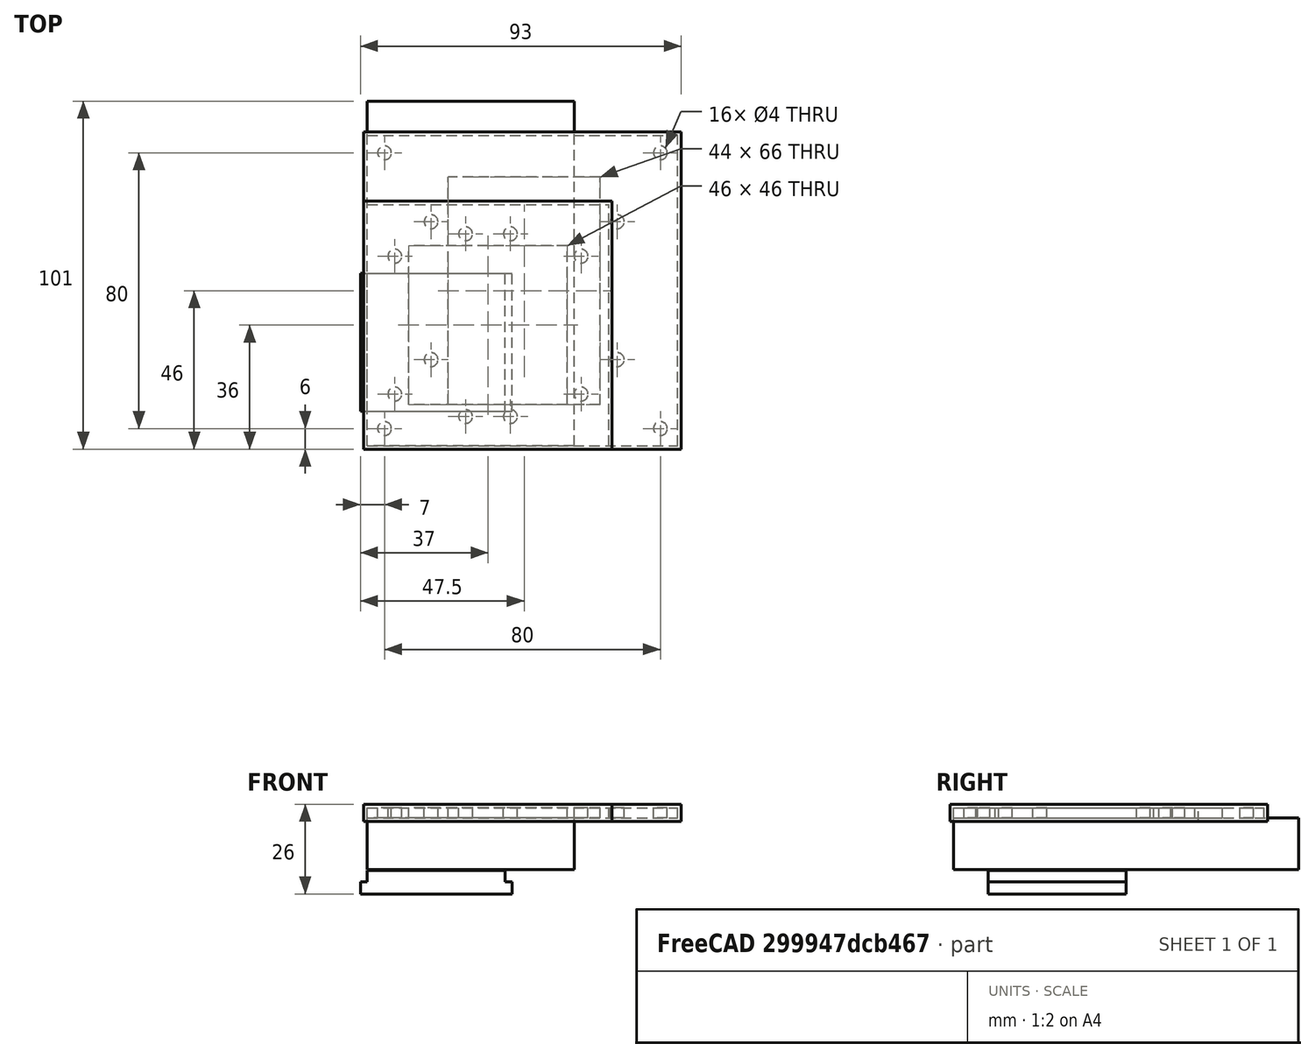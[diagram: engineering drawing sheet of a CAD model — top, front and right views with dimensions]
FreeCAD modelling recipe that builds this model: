
FCSTD DOCUMENT  (FreeCAD 0.18.4R)
Label: box_with_cone
License: All rights reserved
LicenseURL: http://en.wikipedia.org/wiki/All_rights_reserved
objects: Path::FeaturePython×20, Part::FeaturePython×12, Part::Box×8, Part::Cut×6, Part::Cylinder×5, Part::MultiFuse×4, App::Part×4, App::FeaturePython×3, App::DocumentObjectGroup×3, Path::FeatureCompoundPython×3, Part::Cone×2, Part::Feature×2, Part::Fuse×1
note: 47 computed .brp shape members not serialized (recipe doc carries the construction recipe); baked Part::Feature solids carry a one-line shape summary decoded from their .brp

FEATURE [Part::Box] Box  label="Cube"
  AttacherType = Attacher::AttachEngine3D
  Height = 15
  Length = 40
  Placement = pos=(0,0,-15) rot=(0,0,1;0rad)
  Width = 60
FEATURE [Part::Cone] Cone  label="top cone"
  Angle = 360
  AttacherType = Attacher::AttachEngine3D
  Height = 7
  Placement = pos=(0,0,-7) rot=(0,0,1;0rad)
  Radius1 = 2.8
  Radius2 = 3
FEATURE [Part::Cone] Cone001  label="bottom cone"
  Angle = 360
  AttacherType = Attacher::AttachEngine3D
  Height = 12
  Placement = pos=(0,0,-19) rot=(0,0,1;3.14159rad)
  Radius1 = 1.2
  Radius2 = 2.8
  Support = -> [Cone]
FEATURE [Part::Cylinder] Cylinder001
  Angle = 360
  AttacherType = Attacher::AttachEngine3D
  Height = 30
  Placement = pos=(0,0,-20) rot=(0,0,1;0rad)
  Radius = 1.65
FEATURE [Part::FeaturePython] Array002  # Draft array (typed FeaturePython)
  Angle = 360
  ArrayType = 0
  Axis = (0,0,1)
  Base = -> Cylinder001
  Center = (0,0,0)
  Fuse = false
  IntervalAxis = (0,0,0)
  IntervalX = (13,0,0)
  IntervalY = (0,53,0)
  IntervalZ = (0,0,1)
  NumberPolar = 1
  NumberX = 2
  NumberY = 2
  NumberZ = 1
  Placement = pos=(13.5,3.5,0) rot=(0,0,1;0rad)
FEATURE [Part::Fuse] Fusion
  Base = -> Cone001
  Placement = pos=(0,0,5) rot=(0,0,1;0rad)
  Tool = -> Cone
FEATURE [Part::FeaturePython] Array  label="cone array"  # Draft array (typed FeaturePython)
  Angle = 360
  ArrayType = 0
  Axis = (0,0,1)
  Base = -> Fusion
  Center = (0,0,0)
  Fuse = false
  IntervalAxis = (0,0,0)
  IntervalX = (13,0,0)
  IntervalY = (0,13,0)
  IntervalZ = (0,0,1)
  NumberPolar = 1
  NumberX = 3
  NumberY = 4
  NumberZ = 1
  Placement = pos=(7,10,0) rot=(0,0,1;0rad)
FEATURE [Part::Cut] Cut  label="cut cones"
  Base = -> Box
  Tool = -> Array
FEATURE [Part::Box] Box001  label="aluminium solid"
  AttacherType = Attacher::AttachEngine3D
  Height = 15
  Length = 100
  Placement = pos=(0,0,-15) rot=(0,0,1;0rad)
  Width = 60
FEATURE [App::FeaturePython] SetupSheet  # Path/CAM operation (typed FeaturePython)
  ClearanceHeightExpression = OpStockZMax+SetupSheet.ClearanceHeightOffset
  ClearanceHeightOffset = 5
  FinalDepthExpression = OpFinalDepth
  HorizRapid = 100
  SafeHeightExpression = OpStockZMax+SetupSheet.SafeHeightOffset
  SafeHeightOffset = 3
  StartDepthExpression = OpStartDepth
  StepDownExpression = OpToolDiameter
  VertRapid = 100
FEATURE [Path::FeaturePython] T2__drill_3  label="T2: drill 3"  # Path/CAM operation (typed FeaturePython)
  HorizFeed = 0.5
  HorizRapid = 100
  SpindleDir = 0
  SpindleSpeed = 1000
  ToolNumber = 2
  VertFeed = 0.5
  VertRapid = 100
  expr: HorizRapid = SetupSheet.HorizRapid
  expr: VertRapid = SetupSheet.VertRapid
FEATURE [Path::FeaturePython] T4__endmill_2mm  label="T4: endmill 2mm"  # Path/CAM operation (typed FeaturePython)
  HorizFeed = 0.1
  HorizRapid = 100
  SpindleDir = 0
  SpindleSpeed = 1000
  ToolNumber = 4
  VertFeed = 0.05
  VertRapid = 100
  expr: HorizRapid = SetupSheet.HorizRapid
  expr: VertRapid = SetupSheet.VertRapid
FEATURE [Part::FeaturePython] Clone004  label="Stock-solid"  # Draft clone (typed FeaturePython)
  AttacherType = Attacher::AttachEngine3D
  Fuse = false
  Objects = -> [Box001]
  PathResource = Stock
  Placement = pos=(60,0,-15) rot=(0,0,1;1.5708rad)
  Scale = (1,1,1)
  StockType = Unknown
FEATURE [Path::FeaturePython] Contour  # Path/CAM operation (typed FeaturePython)
  Active = false
  AreaParams:
    Tolerance = 1e-07
    FitArcs = True
    Simplify = False
    CleanDistance = 0.0
    Accuracy = 0.01
    Unit = 1.0
    MinArcPoints = 4
    MaxArcPoints = 100
    ClipperScale = 10000000.0
    Fill = 0
    Coplanar = 2
    Reorient = True
    Outline = False
    Explode = False
    OpenMode = 0
    Deflection = 0.01
    SubjectFill = 0
    ClipFill = 0
    Offset = 1.0
    ExtraPass = 0
    Stepover = 0.0
    LastStepover = 0.0
    JoinType = 1
    EndType = 0
    MiterLimit = 2.0
    RoundPrecision = 0.0
    PocketMode = 0
    ToolRadius = 1.0
    PocketExtraOffset = 0.0
    PocketStepover = 0.0
    PocketLastStepover = 0.0
    FromCenter = False
    Angle = 45.0
    AngleShift = 0.0
    Shift = 0.0
    Thicken = False
    SectionCount = -1
    Stepdown = 1.0
    SectionOffset = 0.0
    SectionTolerance = 1e-06
    SectionMode = 2
    Project = False
  ClearanceHeight = 5
  Direction = 0
  FinalDepth = -16
  JoinType = 1
  MiterLimit = 0.1
  OffsetExtra = 0
  OpFinalDepth = -15
  OpStartDepth = 0
  OpStockZMax = 0
  OpStockZMin = -15
  OpToolDiameter = 2
  PathParams = {'orientation': 1, 'feedrate': 0.5, 'feedrate_v': 0.5, 'verbose': True, 'resume_height': 3.0, 'retraction': 5.0, 'return_end': True, 'preamble': False}
  SafeHeight = 3
  Side = 0
  StartDepth = 0
  StartPoint = (0,0,0)
  StepDown = 1
  ToolController = -> T4__endmill_2mm
  UseComp = true
  UseStartPoint = false
  expr: ClearanceHeight = OpStockZMax + SetupSheet.ClearanceHeightOffset
  expr: SafeHeight = OpStockZMax + SetupSheet.SafeHeightOffset
  expr: StartDepth = OpStartDepth
FEATURE [Part::Box] Box002  label="peltier"
  AttacherType = Attacher::AttachEngine3D
  Height = 3.3
  Length = 40
  Width = 40
FEATURE [Part::Box] Box003  label="radiator"
  AttacherType = Attacher::AttachEngine3D
  Height = 3.5
  Length = 44
  Placement = pos=(-2,0,-3.5) rot=(0,0,1;0rad)
  Width = 40
FEATURE [Part::Box] Box004  label="Cube001"
  AttacherType = Attacher::AttachEngine3D
  Height = 3
  Length = 90
  Width = 90
FEATURE [Part::Cylinder] Cylinder002  label="ring bolt hole"
  Angle = 360
  AttacherType = Attacher::AttachEngine3D
  Height = 50
  Radius = 2
FEATURE [Part::FeaturePython] Array003  label="ring holes array"  # Draft array (typed FeaturePython)
  Angle = 360
  ArrayType = 0
  Axis = (0,0,1)
  Base = -> Cylinder002
  Center = (0,0,0)
  Fuse = false
  IntervalAxis = (0,0,0)
  IntervalX = (80,0,0)
  IntervalY = (0,80,0)
  IntervalZ = (0,0,1)
  NumberPolar = 1
  NumberX = 2
  NumberY = 2
  NumberZ = 1
  Placement = pos=(5,5,-25) rot=(0,0,1;0rad)
FEATURE [Part::Box] Box005  label="Cube002"
  AttacherType = Attacher::AttachEngine3D
  Height = 50
  Length = 44
  Placement = pos=(23.5,12,-20) rot=(0,0,1;0rad)
  Width = 66
FEATURE [Part::Cut] Cut002  label="radiator ring plate cut"
  Base = -> Box004
  Tool = -> Box005
FEATURE [Part::Box] Box006  label="Cube003"
  AttacherType = Attacher::AttachEngine3D
  Height = 3
  Length = 70
  Width = 70
FEATURE [Part::Box] Box007  label="Cube004"
  AttacherType = Attacher::AttachEngine3D
  Height = 50
  Length = 46
  Placement = pos=(12,12,-20) rot=(0,0,1;0rad)
  Width = 46
FEATURE [Part::Cut] Cut004  label="block attachment plate cut"
  Base = -> Box006
  Tool = -> Box007
FEATURE [Part::MultiFuse] Fusion003  label="peltier and radiator"
  Placement = pos=(0,10,-18.5) rot=(0,0,1;0rad)
  Shapes = -> [Box002,Box003]
FEATURE [Part::FeaturePython] Array007  label="radiator plate holes"  # Draft array (typed FeaturePython)
  Angle = 360
  ArrayType = 0
  Axis = (0,0,1)
  Center = (0,0,0)
  Fuse = false
  IntervalAxis = (0,0,0)
  IntervalX = (54,0,0)
  IntervalY = (0,40,0)
  IntervalZ = (0,0,1)
  NumberPolar = 1
  NumberX = 2
  NumberY = 2
  NumberZ = 1
  Placement = pos=(8,15,-19) rot=(0,0,1;0rad)
FEATURE [Part::FeaturePython] Array006  label="plate cone box hole array001"  # Draft array (typed FeaturePython)
  Angle = 360
  ArrayType = 0
  Axis = (0,0,1)
  Center = (0,0,0)
  Fuse = false
  IntervalAxis = (0,0,0)
  IntervalX = (13,0,0)
  IntervalY = (0,53,0)
  IntervalZ = (0,0,1)
  NumberPolar = 1
  NumberX = 2
  NumberY = 2
  NumberZ = 1
  Placement = pos=(28.5,8.5,-19) rot=(0,0,1;0rad)
FEATURE [Part::MultiFuse] Fusion004  label="block attachment holes"
  Shapes = -> [Array006,Array007]
FEATURE [Part::Cut] Cut005  label="block attachement all holes cut"
  Base = -> Cut004
  Tool = -> Fusion004
FEATURE [App::Part] Part002  label="block attachment part"
  Group = -> [Box006,Cut004,Box007,Array006,Array007,Fusion004,Cut005]
  Origin = -> Origin002
  Placement = pos=(-15,-5,-18) rot=(0,0,1;0rad)
FEATURE [Part::FeaturePython] Array008  label="radiator plate holes001"  # Draft array (typed FeaturePython)
  Angle = 360
  ArrayType = 0
  Axis = (0,0,1)
  Center = (0,0,0)
  Fuse = false
  IntervalAxis = (0,0,0)
  IntervalX = (54,0,0)
  IntervalY = (0,40,0)
  IntervalZ = (0,0,1)
  NumberPolar = 1
  NumberX = 2
  NumberY = 2
  NumberZ = 1
  Placement = pos=(18.5,25,-19) rot=(0,0,1;0rad)
FEATURE [Part::MultiFuse] Fusion002  label="holes union"
  Shapes = -> [Array003,Array008]
FEATURE [Part::Cut] Cut003  label="radiator block attachment cut"
  Base = -> Cut002
  Tool = -> Fusion002
FEATURE [App::Part] Part  label="radiator block attachment part"
  Group = -> [Box004,Array003,Cut002,Cylinder002,Box005,Fusion002,Cut003]
  Origin = -> Origin
  Placement = pos=(-25.5,-15,-3) rot=(0,0,1;0rad)
FEATURE [Part::Cylinder] Cylinder003  label="ntc_1.8"
  Angle = 360
  AttacherType = Attacher::AttachEngine3D
  Height = 10
  Placement = pos=(27,17,-9) rot=(0,0,1;0rad)
  Radius = 0.9
FEATURE [Part::Cylinder] Cylinder004  label="ntc_2.35"
  Angle = 360
  AttacherType = Attacher::AttachEngine3D
  Height = 10
  Placement = pos=(27,43,-9) rot=(0,0,1;0rad)
  Radius = 1.175
FEATURE [Part::Cylinder] Cylinder005  label="ntc_3"
  Angle = 360
  AttacherType = Attacher::AttachEngine3D
  Height = 10
  Placement = pos=(13,17,-9) rot=(0,0,1;0rad)
  Radius = 1.5
FEATURE [Part::MultiFuse] Fusion001  label="hole union"
  Shapes = -> [Array002,Cylinder003,Cylinder004,Cylinder005]
FEATURE [Part::Cut] Cut001  label="All cut"
  Base = -> Cut
  Tool = -> Fusion001
FEATURE [Part::FeaturePython] Clone  label="Model-All cut"  # Draft clone (typed FeaturePython)
  AttacherType = Attacher::AttachEngine3D
  Fuse = false
  Objects = -> [Cut001]
  PathResource = Model
  Placement = pos=(60,0,0) rot=(0,0,1;1.5708rad)
  Scale = (1,1,1)
FEATURE [App::DocumentObjectGroup] Model
  Group = -> [Clone]
FEATURE [Path::FeaturePython] Pocket_3D  # Path/CAM operation (typed FeaturePython)
  Active = false
  AreaParams:
    Tolerance = 1e-07
    FitArcs = True
    Simplify = False
    CleanDistance = 0.0
    Accuracy = 0.01
    Unit = 1.0
    MinArcPoints = 4
    MaxArcPoints = 100
    ClipperScale = 10000000.0
    Fill = 0
    Coplanar = 0
    Reorient = True
    Outline = False
    Explode = False
    OpenMode = 0
    Deflection = 0.01
    SubjectFill = 0
    ClipFill = 0
    Offset = 0.0
    ExtraPass = 0
    Stepover = 0.0
    LastStepover = 0.0
    JoinType = 0
    EndType = 0
    MiterLimit = 2.0
    RoundPrecision = 0.0
    PocketMode = 3
    ToolRadius = 1.0
    PocketExtraOffset = 0.0
    PocketStepover = 2.0
    PocketLastStepover = 0.0
    FromCenter = True
    Angle = 45.0
    AngleShift = 0.0
    Shift = 0.0
    Thicken = False
    SectionCount = -1
    Stepdown = 1.0
    SectionOffset = 0.0
    SectionTolerance = 1e-06
    SectionMode = 2
    Project = False
  Base = -> [Clone]
  ClearanceHeight = 5
  CutMode = 0
  ExtraOffset = 0
  FinalDepth = -2
  FinishDepth = 0
  KeepToolDown = true
  MinTravel = false
  OffsetPattern = 2
  OpFinalDepth = -2
  OpStartDepth = 0
  OpStockZMax = 0
  OpStockZMin = -15
  OpToolDiameter = 2
  PathParams = {'orientation': 1, 'feedrate': 0.5, 'feedrate_v': 0.5, 'verbose': True, 'resume_height': 3.0, 'retraction': 5.0, 'return_end': True, 'preamble': False, 'threshold': 2.001, 'start': Vector (34.87061227627158, 37.332291129902295, -3.999999)}
  SafeHeight = 3
  StartAt = 0
  StartDepth = 0
  StartPoint = (0,0,0)
  StepDown = 0.25
  StepOver = 100
  ToolController = -> T4__endmill_2mm
  UseStartPoint = false
  ZigZagAngle = 45
  expr: ClearanceHeight = OpStockZMax + SetupSheet.ClearanceHeightOffset
  expr: SafeHeight = OpStockZMax + SetupSheet.SafeHeightOffset
  expr: FinalDepth = OpFinalDepth
  expr: StartDepth = OpStartDepth
FEATURE [Path::FeaturePython] Pocket_3D001  # Path/CAM operation (typed FeaturePython)
  Active = true
  AreaParams:
    Tolerance = 1e-07
    FitArcs = True
    Simplify = False
    CleanDistance = 0.0
    Accuracy = 0.01
    Unit = 1.0
    MinArcPoints = 4
    MaxArcPoints = 100
    ClipperScale = 10000000.0
    Fill = 0
    Coplanar = 0
    Reorient = True
    Outline = False
    Explode = False
    OpenMode = 0
    Deflection = 0.01
    SubjectFill = 0
    ClipFill = 0
    Offset = 0.0
    ExtraPass = 0
    Stepover = 0.0
    LastStepover = 0.0
    JoinType = 0
    EndType = 0
    MiterLimit = 2.0
    RoundPrecision = 0.0
    PocketMode = 3
    ToolRadius = 1.0
    PocketExtraOffset = -0.3
    PocketStepover = 2.0
    PocketLastStepover = 0.0
    FromCenter = False
    Angle = 45.0
    AngleShift = 0.0
    Shift = 0.0
    Thicken = False
    SectionCount = -1
    Stepdown = 1.0
    SectionOffset = 0.0
    SectionTolerance = 1e-06
    SectionMode = 2
    Project = False
  Base = -> [Clone]
  ClearanceHeight = 2
  CutMode = 0
  ExtraOffset = -0.3
  FinalDepth = -14
  FinishDepth = 0
  KeepToolDown = true
  MinTravel = false
  OffsetPattern = 2
  OpFinalDepth = -14
  OpStartDepth = 0
  OpStockZMax = 0
  OpStockZMin = -15
  OpToolDiameter = 2
  PathParams = {'orientation': 1, 'feedrate': 0.1, 'feedrate_v': 0.05, 'verbose': True, 'resume_height': 2.0, 'retraction': 2.0, 'return_end': True, 'preamble': False, 'threshold': 2.001}
  SafeHeight = 2
  StartAt = 1
  StartDepth = -0.1
  StartPoint = (0,0,0)
  StepDown = 0.4
  StepOver = 100
  ToolController = -> T4__endmill_2mm
  UseStartPoint = false
  ZigZagAngle = 45
  expr: FinalDepth = OpFinalDepth
FEATURE [Path::FeaturePython] Drilling  # Path/CAM operation (typed FeaturePython)
  Active = false
  AddTipLength = false
  Base = -> [Clone]
  ClearanceHeight = 5
  DwellEnabled = false
  DwellTime = 0
  FinalDepth = -16
  OpFinalDepth = 0
  OpStartDepth = 1
  OpStockZMax = 0
  OpStockZMin = -15
  OpToolDiameter = 3
  PeckDepth = 5
  PeckEnabled = true
  RetractHeight = 2
  ReturnLevel = 0
  SafeHeight = 3
  StartDepth = -5
  ToolController = -> T2__drill_3
  expr: ClearanceHeight = OpStockZMax + SetupSheet.ClearanceHeightOffset
  expr: SafeHeight = OpStockZMax + SetupSheet.SafeHeightOffset
FEATURE [Path::FeatureCompoundPython] Operations  # Path/CAM operation (typed FeaturePython)
  Group = -> [Contour,Pocket_3D,Pocket_3D001,Drilling]
  UsePlacements = false
FEATURE [Path::FeaturePython] Job  # Path/CAM operation (typed FeaturePython)
  GeometryTolerance = 0.01
  Model = -> Model
  Operations = -> Operations
  PostProcessor = 1
  PostProcessorOutputFile = <userpath>/work/roborep/gcode
  SetupSheet = -> SetupSheet
  Stock = -> Clone004
  ToolController = -> [T2__drill_3,T4__endmill_2mm]
FEATURE [App::Part] Part001  label="cone block"
  Group = -> [Cone,Cylinder001,Fusion,Cut,Fusion001,Cone001,Box,Array,Array002,Cut001,Cylinder003,Cylinder004,Cylinder005]
  Origin = -> Origin001
FEATURE [App::Part] Part003  label="part for all"
  Group = -> [Part,Part001,Part002,Box002,Box003,Fusion003]
  Origin = -> Origin003
  Placement = pos=(60,0,0) rot=(0,0,1;1.5708rad)
FEATURE [Part::Feature] Cut003_solid  label="radiator block attachment cut (Solid)"
  shape: bbox 90 x 90 x 3 mm, 18 faces (baked)
FEATURE [App::FeaturePython] SetupSheet001  # Path/CAM operation (typed FeaturePython)
  ClearanceHeightExpression = OpStockZMax+SetupSheet001.ClearanceHeightOffset
  ClearanceHeightOffset = 5
  FinalDepthExpression = OpFinalDepth
  HorizRapid = 10
  SafeHeightExpression = OpStockZMax+SetupSheet001.SafeHeightOffset
  SafeHeightOffset = 3
  StartDepthExpression = OpStartDepth
  StepDownExpression = OpToolDiameter
  VertRapid = 10
FEATURE [Part::FeaturePython] Clone005  label="Model-radiator block attachment cut (Solid)"  # Draft clone (typed FeaturePython)
  AttacherType = Attacher::AttachEngine3D
  Fuse = false
  Objects = -> [Cut003_solid]
  PathResource = Model
  Scale = (1,1,1)
FEATURE [App::DocumentObjectGroup] Model001
  Group = -> [Clone005]
FEATURE [Part::FeaturePython] Stock  # WARN: FeaturePython — macro-defined, semantics opaque (R4)
  Base = -> Model001
  ExtXneg = 1
  ExtXpos = 1
  ExtYneg = 1
  ExtYpos = 1
  ExtZneg = 1
  ExtZpos = 1
  StockType = FromBase
FEATURE [Path::FeaturePython] T1__reamer_2  label="T1: reamer 2"  # Path/CAM operation (typed FeaturePython)
  HorizFeed = 0.2
  HorizRapid = 10
  SpindleDir = 0
  SpindleSpeed = 1000
  ToolNumber = 1
  VertFeed = 0.2
  VertRapid = 10
  expr: HorizRapid = SetupSheet001.HorizRapid
  expr: VertRapid = SetupSheet001.VertRapid
FEATURE [Path::FeaturePython] T2__drill_3001  label="T2: drill 004"  # Path/CAM operation (typed FeaturePython)
  HorizFeed = 0
  HorizRapid = 10
  SpindleDir = 0
  SpindleSpeed = 1000
  ToolNumber = 2
  VertFeed = 0.1
  VertRapid = 10
  expr: HorizRapid = SetupSheet001.HorizRapid
  expr: VertRapid = SetupSheet001.VertRapid
FEATURE [Path::FeaturePython] T3__laser  label="T3: laser"  # Path/CAM operation (typed FeaturePython)
  HorizFeed = 1
  HorizRapid = 10
  SpindleDir = 0
  SpindleSpeed = 1000
  ToolNumber = 3
  VertFeed = 10
  VertRapid = 10
  expr: HorizRapid = SetupSheet001.HorizRapid
  expr: VertRapid = SetupSheet001.VertRapid
FEATURE [Path::FeaturePython] Profile_Edges001  label="Profile_Edges_inside"  # Path/CAM operation (typed FeaturePython)
  Active = false
  AreaParams:
    Tolerance = 1e-07
    FitArcs = True
    Simplify = False
    CleanDistance = 0.0
    Accuracy = 0.01
    Unit = 1.0
    MinArcPoints = 4
    MaxArcPoints = 100
    ClipperScale = 10000000.0
    Fill = 0
    Coplanar = 0
    Reorient = True
    Outline = False
    Explode = False
    OpenMode = 0
    Deflection = 0.01
    SubjectFill = 0
    ClipFill = 0
    Offset = -1.0
    ExtraPass = 0
    Stepover = 0.0
    LastStepover = 0.0
    JoinType = 0
    EndType = 0
    MiterLimit = 2.0
    RoundPrecision = 0.0
    PocketMode = 0
    ToolRadius = 1.0
    PocketExtraOffset = 0.0
    PocketStepover = 0.0
    PocketLastStepover = 0.0
    FromCenter = False
    Angle = 45.0
    AngleShift = 0.0
    Shift = 0.0
    Thicken = False
    SectionCount = -1
    Stepdown = 1.0
    SectionOffset = 0.0
    SectionTolerance = 1e-06
    SectionMode = 2
    Project = False
  Base = -> [Clone005]
  ClearanceHeight = 9
  Direction = 0
  FinalDepth = -5
  JoinType = 0
  MiterLimit = 0.1
  OffsetExtra = 0
  OpFinalDepth = 0
  OpStartDepth = 4
  OpStockZMax = 4
  OpStockZMin = -1
  OpToolDiameter = 2
  PathParams = {'orientation': 1, 'feedrate': 0.2, 'feedrate_v': 0.2, 'verbose': True, 'resume_height': 7.0, 'retraction': 9.0, 'return_end': True, 'preamble': False}
  SafeHeight = 7
  Side = 1
  StartDepth = -5
  StartPoint = (0,0,0)
  StepDown = 2
  ToolController = -> T1__reamer_2
  UseComp = true
  UseStartPoint = false
  expr: SafeHeight = OpStockZMax + SetupSheet001.SafeHeightOffset
  expr: StepDown = OpToolDiameter
FEATURE [Path::FeaturePython] Contour001  label="Contour outside"  # Path/CAM operation (typed FeaturePython)
  Active = false
  AreaParams:
    Tolerance = 1e-07
    FitArcs = True
    Simplify = False
    CleanDistance = 0.0
    Accuracy = 0.01
    Unit = 1.0
    MinArcPoints = 4
    MaxArcPoints = 100
    ClipperScale = 10000000.0
    Fill = 0
    Coplanar = 2
    Reorient = True
    Outline = False
    Explode = False
    OpenMode = 0
    Deflection = 0.01
    SubjectFill = 0
    ClipFill = 0
    Offset = 1.0
    ExtraPass = 0
    Stepover = 0.0
    LastStepover = 0.0
    JoinType = 0
    EndType = 0
    MiterLimit = 2.0
    RoundPrecision = 0.0
    PocketMode = 0
    ToolRadius = 1.0
    PocketExtraOffset = 0.0
    PocketStepover = 0.0
    PocketLastStepover = 0.0
    FromCenter = False
    Angle = 45.0
    AngleShift = 0.0
    Shift = 0.0
    Thicken = False
    SectionCount = -1
    Stepdown = 1.0
    SectionOffset = 0.0
    SectionTolerance = 1e-06
    SectionMode = 2
    Project = False
  ClearanceHeight = 9
  Direction = 1
  FinalDepth = -10
  JoinType = 0
  MiterLimit = 0.1
  OffsetExtra = 0
  OpFinalDepth = -1
  OpStartDepth = 4
  OpStockZMax = 4
  OpStockZMin = -1
  OpToolDiameter = 2
  PathParams = {'orientation': 0, 'feedrate': 0.2, 'feedrate_v': 0.2, 'verbose': True, 'resume_height': 7.0, 'retraction': 9.0, 'return_end': True, 'preamble': False, 'start': Vector (0.0, 0.0, 0.0)}
  SafeHeight = 7
  Side = 0
  StartDepth = -10
  StartPoint = (0,0,0)
  StepDown = 2
  ToolController = -> T1__reamer_2
  UseComp = true
  UseStartPoint = true
  expr: ClearanceHeight = OpStockZMax + SetupSheet001.ClearanceHeightOffset
  expr: SafeHeight = OpStockZMax + SetupSheet001.SafeHeightOffset
  expr: StepDown = OpToolDiameter
FEATURE [Path::FeaturePython] Drilling001  # Path/CAM operation (typed FeaturePython)
  Active = false
  AddTipLength = false
  Base = -> [Clone005]
  ClearanceHeight = 9
  DwellEnabled = false
  DwellTime = 0
  FinalDepth = -3
  OpFinalDepth = 3
  OpStartDepth = 4
  OpStockZMax = 4
  OpStockZMin = -1
  OpToolDiameter = 2
  PeckDepth = 0
  PeckEnabled = false
  RetractHeight = 10
  ReturnLevel = 0
  SafeHeight = 7
  StartDepth = 4
  ToolController = -> T1__reamer_2
  expr: ClearanceHeight = OpStockZMax + SetupSheet001.ClearanceHeightOffset
  expr: SafeHeight = OpStockZMax + SetupSheet001.SafeHeightOffset
  expr: StartDepth = OpStartDepth
FEATURE [Path::FeatureCompoundPython] Operations001  # Path/CAM operation (typed FeaturePython)
  Group = -> [Profile_Edges001,Drilling001,Contour001]
  UsePlacements = false
FEATURE [Path::FeaturePython] Job001  label="radiator attachment job"  # Path/CAM operation (typed FeaturePython)
  GeometryTolerance = 0.01
  Model = -> Model001
  Operations = -> Operations001
  PostProcessor = 1
  PostProcessorOutputFile = <userpath>/work/roborep/freecad/cone_hole/radiator_attachment.gcode
  SetupSheet = -> SetupSheet001
  Stock = -> Stock
  ToolController = -> [T1__reamer_2,T2__drill_3001,T3__laser]
FEATURE [Part::Feature] Cut005_solid  label="block attachement all holes cut (Solid)"
  shape: bbox 70 x 70 x 3 mm, 18 faces (baked)
FEATURE [App::FeaturePython] SetupSheet002  # Path/CAM operation (typed FeaturePython)
  ClearanceHeightExpression = OpStockZMax+SetupSheet002.ClearanceHeightOffset
  ClearanceHeightOffset = 5
  FinalDepthExpression = OpFinalDepth
  HorizRapid = 300
  SafeHeightExpression = OpStockZMax+SetupSheet002.SafeHeightOffset
  SafeHeightOffset = 3
  StartDepthExpression = OpStartDepth
  StepDownExpression = OpToolDiameter
  VertRapid = 300
FEATURE [Part::FeaturePython] Clone006  label="Model-block attachement all holes cut (Solid)"  # Draft clone (typed FeaturePython)
  AttacherType = Attacher::AttachEngine3D
  Fuse = false
  Objects = -> [Cut005_solid]
  PathResource = Model
  Scale = (1,1,1)
FEATURE [App::DocumentObjectGroup] Model002
  Group = -> [Clone006]
FEATURE [Part::FeaturePython] Stock001  # WARN: FeaturePython — macro-defined, semantics opaque (R4)
  Base = -> Model002
  ExtXneg = 1
  ExtXpos = 1
  ExtYneg = 1
  ExtYpos = 1
  ExtZneg = 1
  ExtZpos = 1
  StockType = FromBase
FEATURE [Path::FeaturePython] T1__reamer_2001  label="T1: reamer 003"  # Path/CAM operation (typed FeaturePython)
  HorizFeed = 0.5
  HorizRapid = 300
  SpindleDir = 0
  SpindleSpeed = 1000
  ToolNumber = 1
  VertFeed = 0.5
  VertRapid = 300
  expr: HorizRapid = SetupSheet002.HorizRapid
  expr: VertRapid = SetupSheet002.VertRapid
FEATURE [Path::FeaturePython] T2__drill_3002  label="T2: drill 005"  # Path/CAM operation (typed FeaturePython)
  HorizFeed = 0.01
  HorizRapid = 300
  SpindleDir = 0
  SpindleSpeed = 1000
  ToolNumber = 2
  VertFeed = 0.2
  VertRapid = 300
  expr: HorizRapid = SetupSheet002.HorizRapid
  expr: VertRapid = SetupSheet002.VertRapid
FEATURE [Path::FeaturePython] Contour002  # Path/CAM operation (typed FeaturePython)
  Active = true
  AreaParams:
    Tolerance = 1e-07
    FitArcs = True
    Simplify = False
    CleanDistance = 0.0
    Accuracy = 0.01
    Unit = 1.0
    MinArcPoints = 4
    MaxArcPoints = 100
    ClipperScale = 10000000.0
    Fill = 0
    Coplanar = 2
    Reorient = True
    Outline = False
    Explode = False
    OpenMode = 0
    Deflection = 0.01
    SubjectFill = 0
    ClipFill = 0
    Offset = 1.0
    ExtraPass = 0
    Stepover = 0.0
    LastStepover = 0.0
    JoinType = 0
    EndType = 0
    MiterLimit = 2.0
    RoundPrecision = 0.0
    PocketMode = 0
    ToolRadius = 1.0
    PocketExtraOffset = 0.0
    PocketStepover = 0.0
    PocketLastStepover = 0.0
    FromCenter = False
    Angle = 45.0
    AngleShift = 0.0
    Shift = 0.0
    Thicken = False
    SectionCount = -1
    Stepdown = 1.0
    SectionOffset = 0.0
    SectionTolerance = 1e-06
    SectionMode = 2
    Project = False
  ClearanceHeight = 9
  Direction = 1
  FinalDepth = -10
  JoinType = 0
  MiterLimit = 0.1
  OffsetExtra = 0
  OpFinalDepth = -1
  OpStartDepth = 4
  OpStockZMax = 4
  OpStockZMin = -1
  OpToolDiameter = 2
  PathParams = {'orientation': 0, 'feedrate': 0.5, 'feedrate_v': 0.5, 'verbose': True, 'resume_height': 7.0, 'retraction': 9.0, 'return_end': True, 'preamble': False, 'start': Vector (0.0, 0.0, 0.0)}
  SafeHeight = 7
  Side = 0
  StartDepth = -10
  StartPoint = (0,0,0)
  StepDown = 2
  ToolController = -> T1__reamer_2001
  UseComp = true
  UseStartPoint = true
  expr: ClearanceHeight = OpStockZMax + SetupSheet002.ClearanceHeightOffset
  expr: SafeHeight = OpStockZMax + SetupSheet002.SafeHeightOffset
FEATURE [Path::FeaturePython] Profile_Edges  # Path/CAM operation (typed FeaturePython)
  Active = false
  AreaParams:
    Tolerance = 1e-07
    FitArcs = True
    Simplify = False
    CleanDistance = 0.0
    Accuracy = 0.01
    Unit = 1.0
    MinArcPoints = 4
    MaxArcPoints = 100
    ClipperScale = 10000000.0
    Fill = 0
    Coplanar = 0
    Reorient = True
    Outline = False
    Explode = False
    OpenMode = 0
    Deflection = 0.01
    SubjectFill = 0
    ClipFill = 0
    Offset = -1.0
    ExtraPass = 0
    Stepover = 0.0
    LastStepover = 0.0
    JoinType = 0
    EndType = 0
    MiterLimit = 2.0
    RoundPrecision = 0.0
    PocketMode = 0
    ToolRadius = 1.0
    PocketExtraOffset = 0.0
    PocketStepover = 0.0
    PocketLastStepover = 0.0
    FromCenter = False
    Angle = 45.0
    AngleShift = 0.0
    Shift = 0.0
    Thicken = False
    SectionCount = -1
    Stepdown = 1.0
    SectionOffset = 0.0
    SectionTolerance = 1e-06
    SectionMode = 2
    Project = False
  Base = -> [Clone006]
  ClearanceHeight = 9
  Direction = 0
  FinalDepth = -10
  JoinType = 0
  MiterLimit = 0.1
  OffsetExtra = 0
  OpFinalDepth = 3
  OpStartDepth = 4
  OpStockZMax = 4
  OpStockZMin = -1
  OpToolDiameter = 2
  PathParams = {'orientation': 1, 'feedrate': 0.5, 'feedrate_v': 0.5, 'verbose': True, 'resume_height': 7.0, 'retraction': 9.0, 'return_end': True, 'preamble': False}
  SafeHeight = 7
  Side = 1
  StartDepth = -10
  StartPoint = (0,0,0)
  StepDown = 2
  ToolController = -> T1__reamer_2001
  UseComp = true
  UseStartPoint = false
  expr: ClearanceHeight = OpStockZMax + SetupSheet002.ClearanceHeightOffset
  expr: SafeHeight = OpStockZMax + SetupSheet002.SafeHeightOffset
  expr: StepDown = OpToolDiameter
FEATURE [Path::FeaturePython] Drilling002  # Path/CAM operation (typed FeaturePython)
  Active = false
  AddTipLength = false
  Base = -> [Clone006]
  ClearanceHeight = 9
  DwellEnabled = false
  DwellTime = 0
  FinalDepth = -10
  OpFinalDepth = 0
  OpStartDepth = 4
  OpStockZMax = 4
  OpStockZMin = -1
  OpToolDiameter = 3
  PeckDepth = 0
  PeckEnabled = false
  RetractHeight = 10
  ReturnLevel = 0
  SafeHeight = 7
  StartDepth = 0
  ToolController = -> T2__drill_3002
  expr: ClearanceHeight = OpStockZMax + SetupSheet002.ClearanceHeightOffset
  expr: SafeHeight = OpStockZMax + SetupSheet002.SafeHeightOffset
FEATURE [Path::FeatureCompoundPython] Operations002  # Path/CAM operation (typed FeaturePython)
  Group = -> [Contour002,Profile_Edges,Drilling002]
  UsePlacements = false
FEATURE [Path::FeaturePython] Job002  label="block attachment all holes job"  # Path/CAM operation (typed FeaturePython)
  GeometryTolerance = 0.01
  Model = -> Model002
  Operations = -> Operations002
  PostProcessor = 1
  PostProcessorOutputFile = <userpath>/work/roborep/gcode
  SetupSheet = -> SetupSheet002
  Stock = -> Stock001
  ToolController = -> [T1__reamer_2001,T2__drill_3002]
